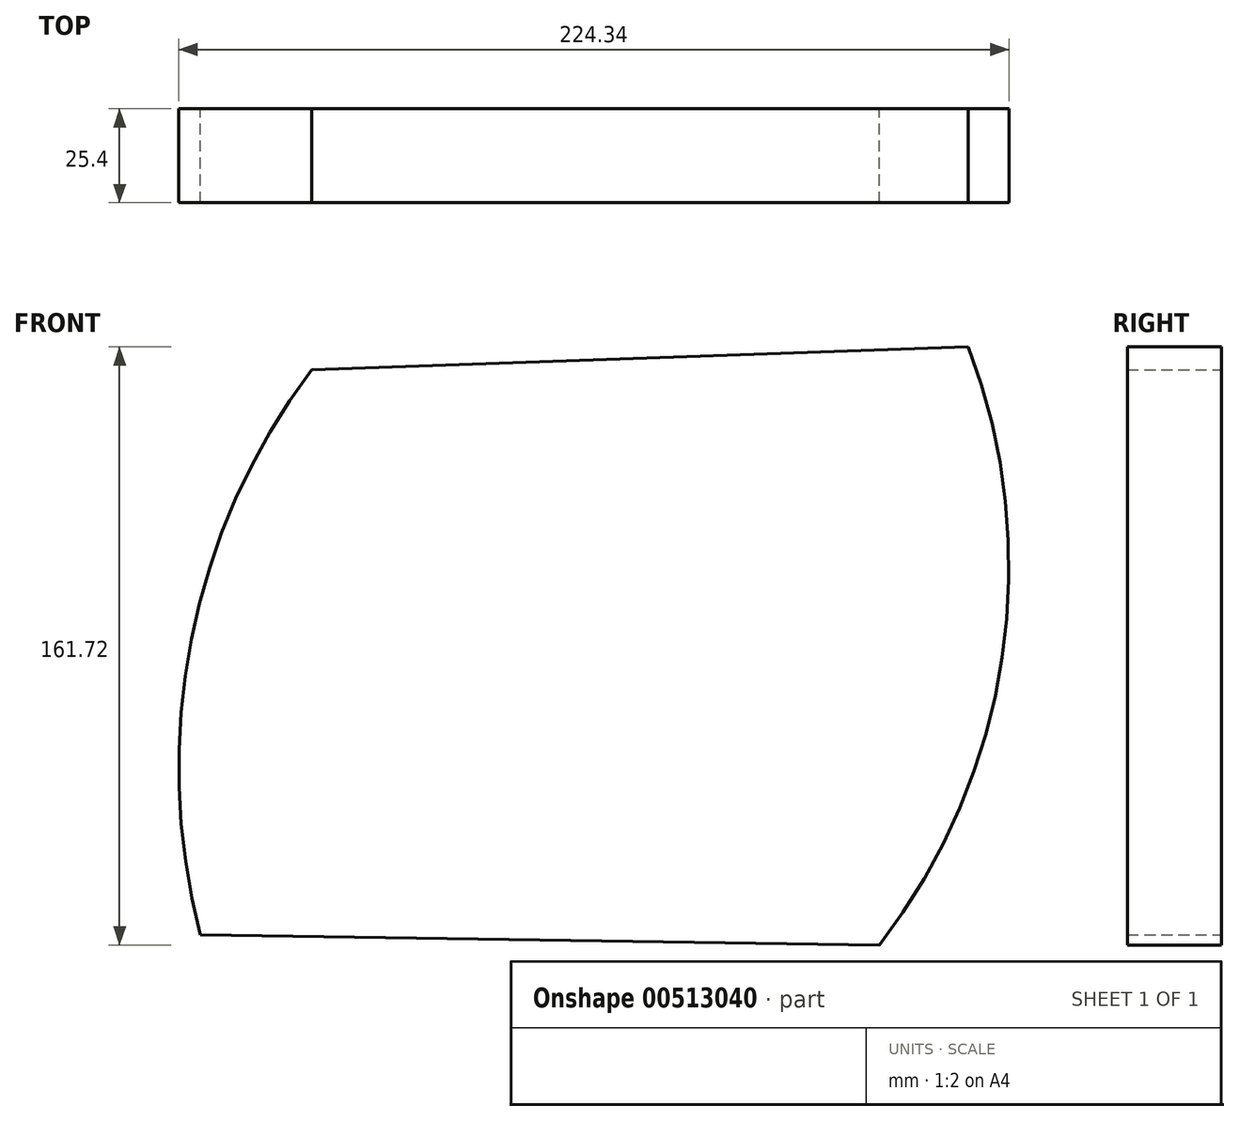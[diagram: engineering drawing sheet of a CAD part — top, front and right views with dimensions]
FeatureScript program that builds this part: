
annotation { "Feature Type Name" : "Feature", "Feature Type Description" : "" }
export const myFeature = defineFeature(function(context is Context, id is Id, definition is map)
    precondition{}
    {
        {
            var Q0;
            Q0=qCreatedBy(makeId("Front.planeOp"),FACE);
            var sketch = newSketch(context, id + "F0", { "sketchPlane" : qUnion([Q0])});
            skArc(sketch, "E0", {"start": v(-89.4, 72.27) * mm, "mid": v(-121.94, -0.68) * mm, "end": v(-119.43, -80.51) * mm});
            skArc(sketch, "E1", {"start": v(64.05, -83.26) * mm, "mid": v(97.24, -5.54) * mm, "end": v(88.07, 78.46) * mm});
            skLineSegment(sketch, "E2", {"start": v(-89.4, 72.27) * mm, "end": v(88.07, 78.46) * mm});
            skLineSegment(sketch, "E3", {"start": v(-119.43, -80.51) * mm, "end": v(64.05, -83.26) * mm});
            skSolve(sketch);
        }
        {
            var Q0;
            Q0 = qSketchRegion(id + "F0", true);
            extrude(context, id + "F1", {"entities" : qUnion([Q0]), "depth" : 25.4 * mm});
        }
    });
